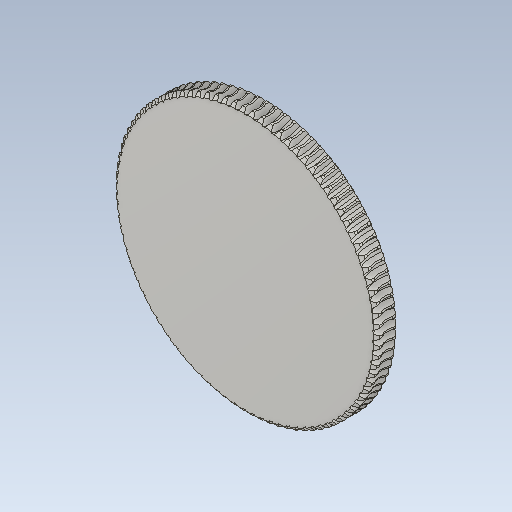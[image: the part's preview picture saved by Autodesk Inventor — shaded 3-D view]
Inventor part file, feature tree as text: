
AUTODESK INVENTOR PART (.ipt)
format: ipt  version: 2021 (Build 250183000, 183)  size: 1,734,656 bytes
history: native  units: mm (DEFAULTED — no unit token found)
features: other x8, plane x3, pattern_circular x1, sketch x1
ambient origin geometry x5: Origin, X Axis, Y Axis, Z Axis, Center Point
bodies: Solid1 (feature_tree)
feature tree (13):
  other  "Tooth Plane"
  other  "Base Body Sketch"
  other  "Base Body"
  other  "Base Body2"
  plane  "Work Plane13"
  other  "Tooth"
  pattern_circular  "Tooth Pattern"  [2 undecoded]
  plane  "Work Plane14"
  plane  "Work Plane15"
  other  "Tooth Sketch"
  sketch  "Sketch8"  dims[d35=90.0deg d37=-0.996687mm d38=80.850711mm d39=3.490659mm d40=6.144654mm d41=8.085071mm d42=1.524mm d43=90.0deg d44=900.0mm d46=360.0deg d50=6.865652mm d68=80.850711mm d69=0.0mm d73=0.0mm d75=0.349066mm d77=145.53128mm d78=12.3mm d79=0.0mm d80=0.0mm d81=0.0mm d82=0.0mm d83=0.349066mm d84=0.0mm d85=180.0deg d86=80.850711mm d87=150.382323mm d89=12.936114mm d90=90.0deg d92=12.3mm d93=80.850711mm]
  other  "Srf1"
  other  "Pitch Diameter"
note: 2 required parameter values undecoded (feature->parameter linkage not recoverable at this tier; creation-order binding heuristic only, values carry confidence <= 0.55)
